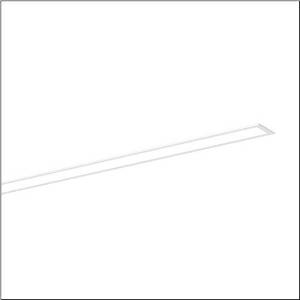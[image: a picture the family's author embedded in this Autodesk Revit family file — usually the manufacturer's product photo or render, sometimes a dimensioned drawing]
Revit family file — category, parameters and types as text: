
# Revit family: silica_21_51mx10tbt2w
name_source: partatom
category: Lighting Fixtures
units: mm (PartAtom-declared; Revit-internal decimal feet)

## family parameters
Cut with Voids When Loaded = No
Host = Face
Light Source = No
Part Type = Normal
Room Calculation Point = No
Round Connector Dimension = Use Diameter
Shared = No

## types (1)
- --- (1 x LED, 3000 lm, 25.6 W, 6500K)
    Apparent Load = 26 VA
    CIE Flux Codes = 48 79 96 100 100
    Color Rendering = 80
    Color Temperature = 6500K
    Default Elevation = 1800 mm
    Description = Silica 21, office luminaire, primary optical cover: cover, of PMMA, opal, light emission: direct distribution, primary light characteristic: symmetric, installation type: recessed, LED, rated luminous flux: 3.000lm, luminous efficacy: 112lm/W, light colour: 8tw, colour temperature: 2700..6500K, control gear: DALI DT8, with terminal, 3+2-pole, max. 2.5mm², mains connection: 220..240V, AC, 50/60Hz, rated input power: 26.9W, luminaire housing, of aluminium, traffic white (RAL 9016), length: 1.528mm, width: 77mm, height: 53mm, protection rating (complete): IP20, insulation class (complete): insulation class I (protective earthing), certification: CE, ENEC, VDE, permissible operating ambient temperature: 0..+35°C, standard: EN 50419, packaging unit: 1 piece
    Height = 0 mm  [stored 0 ft]
    Lamp = 1 x LED
    Lamp Light Flux = 3000 lm
    Lamp Power = 25.6 W
    Lamp count = 1
    Length = 1527 mm
    Luminous efficacy = 117 lm/W
    Manufacturer = Siteco
    ModVariant = No
    Model = 51MX10TBT2W
    Mounting Place = Ceiling
    Mounting Type = Recessed
    Number of Poles = 1
    OnlyDefault = Yes
    Power Factor = 1
    Product Name = Silica 21
    Product group = office luminaire | ceiling recessed
    ProductGroupID = 400
    Protection Class = Protection class I
    Protection Degree = IP 20
    RLX_Detail_Level = 1
    RLX_Emergency_Light_Flux = 0 lm
    RLX_Emergency_Type = 0
    RLX_Emergency_Type_DB = No
    RlxData = <blob elided: 17985 chars, md5=42179087>
    Socket = socket
    Standby Power = 0 W
    System Light Flux = 3000 lm
    System Power = 26 W
    Type Comments = individual setting
    Type Image = l_1335891.jpg
    URL = http://relux.com
    VarID = @adj_139217
    Voltage = 0 V
    Weight = 0.00 kg
    Width = 79 mm

note: [stored X ft] marks values corroborated as IEEE doubles in the binary element streams (Revit-internal decimal feet)

## geometry (parser evidence)
native form markers: Blend x4, Sweep x10
no freeform markers — native parametric forms only
